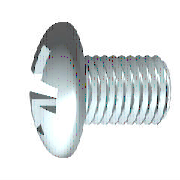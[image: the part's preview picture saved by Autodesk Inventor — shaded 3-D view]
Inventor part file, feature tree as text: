
AUTODESK INVENTOR PART (.ipt)
format: ipt  version: 2019 (Build 230136000, 136)  size: 278,528 bytes
history: native  units: mm (DEFAULTED — no unit token found)
features: other x2, plane x2, extrude x1
ambient origin geometry x7: Origin, YZ Plane, XZ Plane, X Axis, Y Axis, Z Axis, Center Point
bodies: Solid1 (feature_tree)
feature tree (5):
  other  "Cuerpo"
  plane  "Work Plane1"
  extrude  "Ranura"  Depth=4.0mm
  other  "Corte"
  plane  "Work Plane3"
